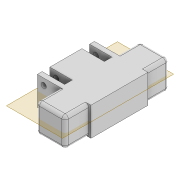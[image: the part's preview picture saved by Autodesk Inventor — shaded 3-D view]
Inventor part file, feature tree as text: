
AUTODESK INVENTOR PART (.ipt)
format: ipt  version: 2022 (Build 260153000, 153)  size: 174,592 bytes
history: native  units: mm
features: extrude x2, sketch x2, fillet x1, plane x1
ambient origin geometry x8: Origin, YZ Plane, XZ Plane, XY Plane, X Axis, Y Axis, Z Axis, Center Point
bodies: Solid1 (feature_tree)
feature tree (6):
  extrude  "Extrusion1"  Depth=3.0mm
  fillet  "Fillet1"  Radius=20.0mm
  extrude  "Extrusion2"  Depth=1.5mm
  plane  "Work Plane1"
  sketch  "Sketch1"  dims[d0=17.9mm d2=3.0mm d4=20.0mm]
  sketch  "Sketch2"  dims[d5=24.8mm d6=2.4mm d7=2.4mm d8=2.4mm d9=2.4mm d10=3.0mm d11=14.0mm d12=17.9mm d13=0.0mm d14=20.0mm d15=2.0mm d16=3.2mm d17=3.2mm d18=10.0mm d19=10.0mm d20=4.0mm d21=4.0mm d22=100.0mm d23=0.0mm d24=1.5mm]
